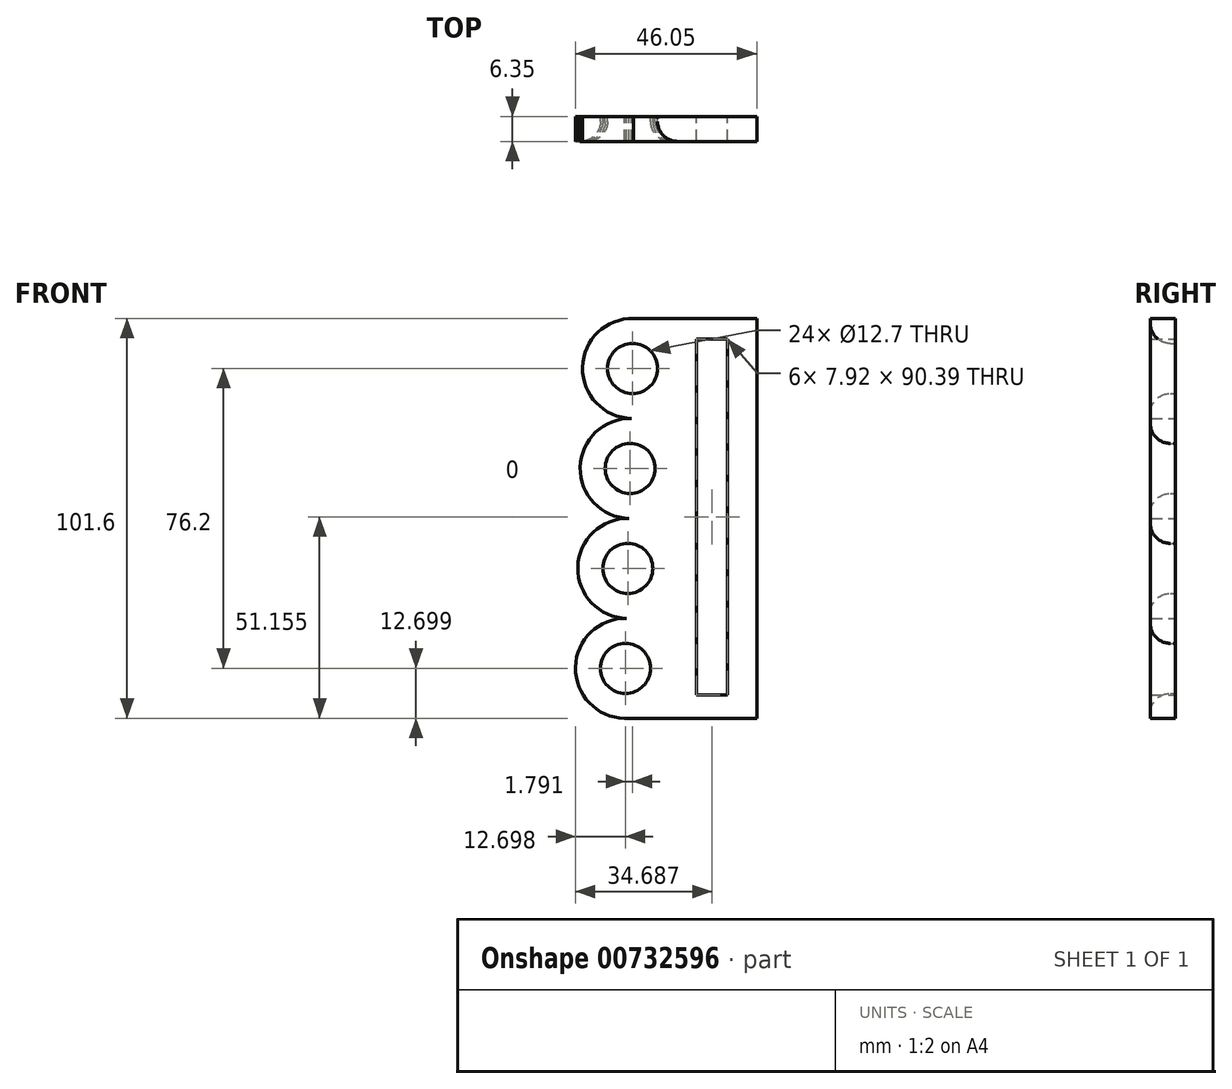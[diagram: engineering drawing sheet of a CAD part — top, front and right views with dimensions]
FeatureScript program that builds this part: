
annotation { "Feature Type Name" : "Feature", "Feature Type Description" : "" }
export const myFeature = defineFeature(function(context is Context, id is Id, definition is map)
    precondition{}
    {
        {
            var Q0;
            Q0=qCreatedBy(makeId("Front.planeOp"),FACE);
            var sketch = newSketch(context, id + "F0", { "sketchPlane" : qUnion([Q0])});
            skLineSegment(sketch, "E0", {"start": v(14.28, 55.9) * mm, "end": v(14.28, -45.7) * mm});
            skLineSegment(sketch, "E1", {"start": v(14.28, -45.7) * mm, "end": v(14.28, 55.9) * mm});
            skLineSegment(sketch, "E2", {"start": v(14.28, 55.9) * mm, "end": v(-16.98, 55.9) * mm});
            skLineSegment(sketch, "E3", {"start": v(14.28, -45.7) * mm, "end": v(-19.37, -45.7) * mm});
            skLineSegment(sketch, "E4", {"start": v(-19.37, -45.7) * mm, "end": v(-19.37, -45.69) * mm});
            skArc(sketch, "E5", {"start": v(-18.77, -20.3) * mm, "mid": v(-31.77, -32.84) * mm, "end": v(-19.07, -45.7) * mm});
            skArc(sketch, "E6", {"start": v(-18.18, 5.1) * mm, "mid": v(-31.17, -7.3) * mm, "end": v(-18.77, -20.29) * mm});
            skArc(sketch, "E7", {"start": v(-17.58, 30.5) * mm, "mid": v(-30.57, 18.1) * mm, "end": v(-18.18, 5.11) * mm});
            skArc(sketch, "E8", {"start": v(-16.98, 55.9) * mm, "mid": v(-29.98, 43.5) * mm, "end": v(-17.58, 30.51) * mm});
            skLineSegment(sketch, "E9.trimOffspring", {"start": v(-18.77, -20.3) * mm, "end": v(-18.77, -20.29) * mm});
            skLineSegment(sketch, "E10.trimOffspring", {"start": v(-18.18, 5.1) * mm, "end": v(-18.18, 5.11) * mm});
            skLineSegment(sketch, "E11.trimOffspring", {"start": v(-17.58, 30.5) * mm, "end": v(-17.58, 30.51) * mm});
            skLineSegment(sketch, "E12.trimOffspring", {"start": v(-16.98, 55.9) * mm, "end": v(-16.98, 55.9) * mm});
            skCircle(sketch, "E13", {"center": v(-19.07, -33) * mm, "radius": 6.35 * mm});
            skCircle(sketch, "E14", {"center": v(-18.48, -7.6) * mm, "radius": 6.35 * mm});
            skCircle(sketch, "E15", {"center": v(-17.88, 17.8) * mm, "radius": 6.35 * mm});
            skCircle(sketch, "E16", {"center": v(-17.28, 43.2) * mm, "radius": 6.35 * mm});
            skLineSegment(sketch, "E17.bottom", {"start": v(-1.05, -39.73) * mm, "end": v(6.88, -39.73) * mm});
            skLineSegment(sketch, "E17.top", {"start": v(-1.05, 50.66) * mm, "end": v(6.88, 50.66) * mm});
            skLineSegment(sketch, "E17.left", {"start": v(-1.05, -39.73) * mm, "end": v(-1.05, 50.66) * mm});
            skLineSegment(sketch, "E17.right", {"start": v(6.88, -39.73) * mm, "end": v(6.88, 50.66) * mm});
            skSolve(sketch);
        }
        {
            var Q0;
            Q0 = qSketchRegion(id + "F0", true);
            extrude(context, id + "F1", {"entities" : qUnion([Q0]), "depth" : 6.35 * mm, "offsetDistance" : 25.4 * mm});
        }
        {
            var Q0;
            Q0=makeQuery(id+"F1.opExtrude","CAP_EDGE",EDGE,{"disambiguationData":[OSD([sQuery(id+"F0.wireOp",EDGE,"E16")])],"isStart":false});
            var Q1;
            Q1=makeQuery(id+"F1.opExtrude","CAP_EDGE",EDGE,{"disambiguationData":[OSD([sQuery(id+"F0.wireOp",EDGE,"E15")])],"isStart":false});
            var Q2;
            Q2=makeQuery(id+"F1.opExtrude","CAP_EDGE",EDGE,{"disambiguationData":[OSD([sQuery(id+"F0.wireOp",EDGE,"E14")])],"isStart":false});
            var Q3;
            Q3=makeQuery(id+"F1.opExtrude","CAP_EDGE",EDGE,{"disambiguationData":[OSD([sQuery(id+"F0.wireOp",EDGE,"E13")])],"isStart":false});
            fillet(context, id + "F2", {"entities" : qUnion([Q0, Q1, Q2, Q3]), "radius" : 5.08 * mm, "tangentPropagation" : true, "allowEdgeOverflow" : false});
        }
        {
            var Q0;
            Q0=makeQuery(id+"F1.opExtrude","CAP_EDGE",EDGE,{"disambiguationData":[OSD([sQuery(id+"F0.wireOp",EDGE,"E13")])],"isStart":true});
            var Q1;
            Q1=makeQuery(id+"F1.opExtrude","CAP_EDGE",EDGE,{"disambiguationData":[OSD([sQuery(id+"F0.wireOp",EDGE,"E14")])],"isStart":true});
            var Q2;
            Q2=makeQuery(id+"F1.opExtrude","CAP_EDGE",EDGE,{"disambiguationData":[OSD([sQuery(id+"F0.wireOp",EDGE,"E15")])],"isStart":true});
            var Q3;
            Q3=makeQuery(id+"F1.opExtrude","CAP_EDGE",EDGE,{"disambiguationData":[OSD([sQuery(id+"F0.wireOp",EDGE,"E16")])],"isStart":true});
            fillet(context, id + "F3", {"entities" : qUnion([Q0, Q1, Q2, Q3]), "radius" : 0.5 * mm, "tangentPropagation" : true, "allowEdgeOverflow" : false});
        }
    });
